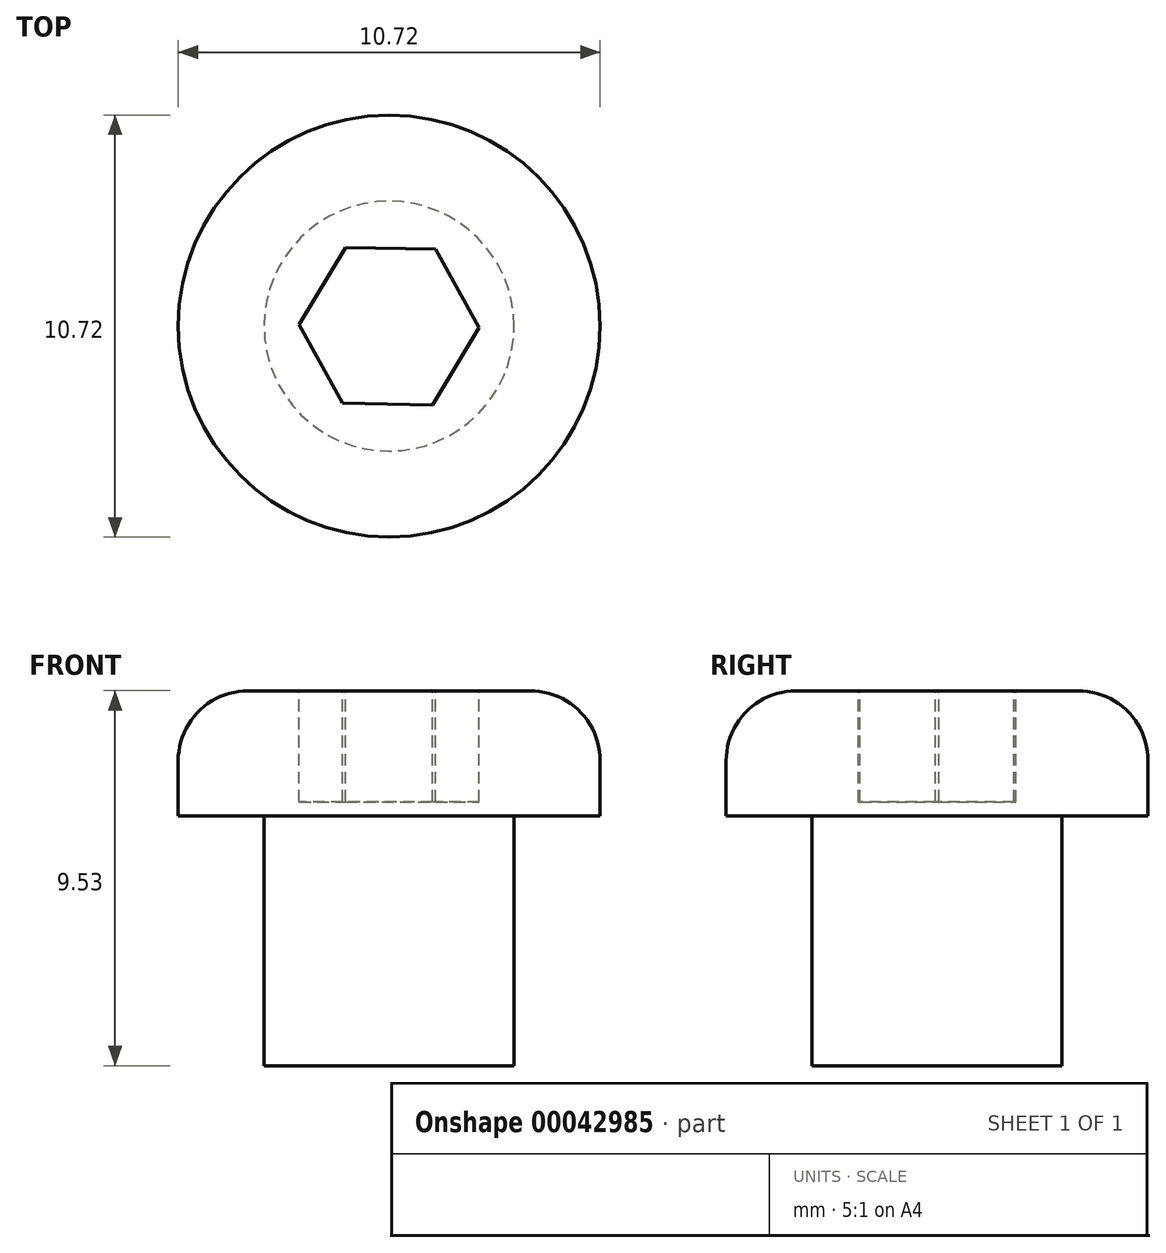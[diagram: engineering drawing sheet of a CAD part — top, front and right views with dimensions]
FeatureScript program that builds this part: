
annotation { "Feature Type Name" : "Feature", "Feature Type Description" : "" }
export const myFeature = defineFeature(function(context is Context, id is Id, definition is map)
    precondition{}
    {
        {
            var Q0;
            Q0=qCreatedBy(makeId("Top.planeOp"),FACE);
            var sketch = newSketch(context, id + "F0", { "sketchPlane" : qUnion([Q0])});
            skCircle(sketch, "E0", {"center": v(0, 0) * mm, "radius": 3.18 * mm});
            skSolve(sketch);
        }
        {
            var Q0;
            Q0 = qSketchRegion(id + "F0", true);
            extrude(context, id + "F1", {"entities" : qUnion([Q0]), "depth" : 6.35 * mm});
        }
        {
            var Q0;
            Q0=makeQuery(id+"F1.opExtrude","CAP_FACE",FACE,{"disambiguationData":[OSD([sQuery(id+"F0.wireOp",EDGE,"E0")])],"isStart":false});
            var sketch = newSketch(context, id + "F2", { "sketchPlane" : qUnion([Q0])});
            skCircle(sketch, "E1", {"center": v(0, 0) * mm, "radius": 5.36 * mm});
            skSolve(sketch);
        }
        {
            var Q0;
            Q0 = qSketchRegion(id + "F2", true);
            extrude(context, id + "F3", {"entities" : qUnion([Q0]), "operationType" : NewBodyOperationType.ADD, "depth" : 0.79 * mm});
        }
        {
            var Q0;
            Q0=makeQuery(id+"F3.opExtrude","CAP_FACE",FACE,{"disambiguationData":[OSD([sQuery(id+"F2.wireOp",EDGE,"E1")])],"isStart":false});
            var sketch = newSketch(context, id + "F4", { "sketchPlane" : qUnion([Q0])});
            skCircle(sketch, "E2", {"center": v(0, 0) * mm, "radius": 5.36 * mm});
            skSolve(sketch);
        }
        {
            var Q0;
            Q0 = qSketchRegion(id + "F4", true);
            extrude(context, id + "F5", {"entities" : qUnion([Q0]), "operationType" : NewBodyOperationType.ADD, "depth" : 2.4 * mm});
        }
        {
            var Q0;
            Q0=makeQuery(id+"F5.opExtrude","CAP_EDGE",EDGE,{"disambiguationData":[OSD([sQuery(id+"F4.wireOp",EDGE,"E2")])],"isStart":false});
            fillet(context, id + "F6", {"entities" : qUnion([Q0]), "radius" : 1.78 * mm, "tangentPropagation" : true, "allowEdgeOverflow" : false});
        }
        {
            var Q0;
            Q0=makeQuery(id+"F5.opExtrude","CAP_FACE",FACE,{"disambiguationData":[OSD([sQuery(id+"F4.wireOp",EDGE,"E2")])],"isStart":false});
            var sketch = newSketch(context, id + "F7", { "sketchPlane" : qUnion([Q0])});
            skCircle(sketch, "E3.cCircle", {"center": v(0, 0) * mm, "radius": 1.98 * mm, "construction": true});
            skLineSegment(sketch, "E3.0", {"start": v(2.29, -0.04) * mm, "end": v(1.1, -2) * mm});
            skLineSegment(sketch, "E3.1", {"start": v(1.1, -2) * mm, "end": v(-1.18, -1.96) * mm});
            skLineSegment(sketch, "E3.2", {"start": v(-1.18, -1.96) * mm, "end": v(-2.29, 0.04) * mm});
            skLineSegment(sketch, "E3.3", {"start": v(-2.29, 0.04) * mm, "end": v(-1.1, 2) * mm});
            skLineSegment(sketch, "E3.4", {"start": v(-1.1, 2) * mm, "end": v(1.18, 1.96) * mm});
            skLineSegment(sketch, "E3.5", {"start": v(1.18, 1.96) * mm, "end": v(2.29, -0.04) * mm});
            skPoint(sketch, "E3.0.midPoint", {"position": v(1.7, -1.02) * mm});
            skSolve(sketch);
        }
        {
            var Q0;
            Q0 = qSketchRegion(id + "F7", true);
            extrude(context, id + "F8", {"entities" : qUnion([Q0]), "operationType" : NewBodyOperationType.REMOVE, "oppositeDirection" : true, "depth" : 2.82 * mm});
        }
    });
